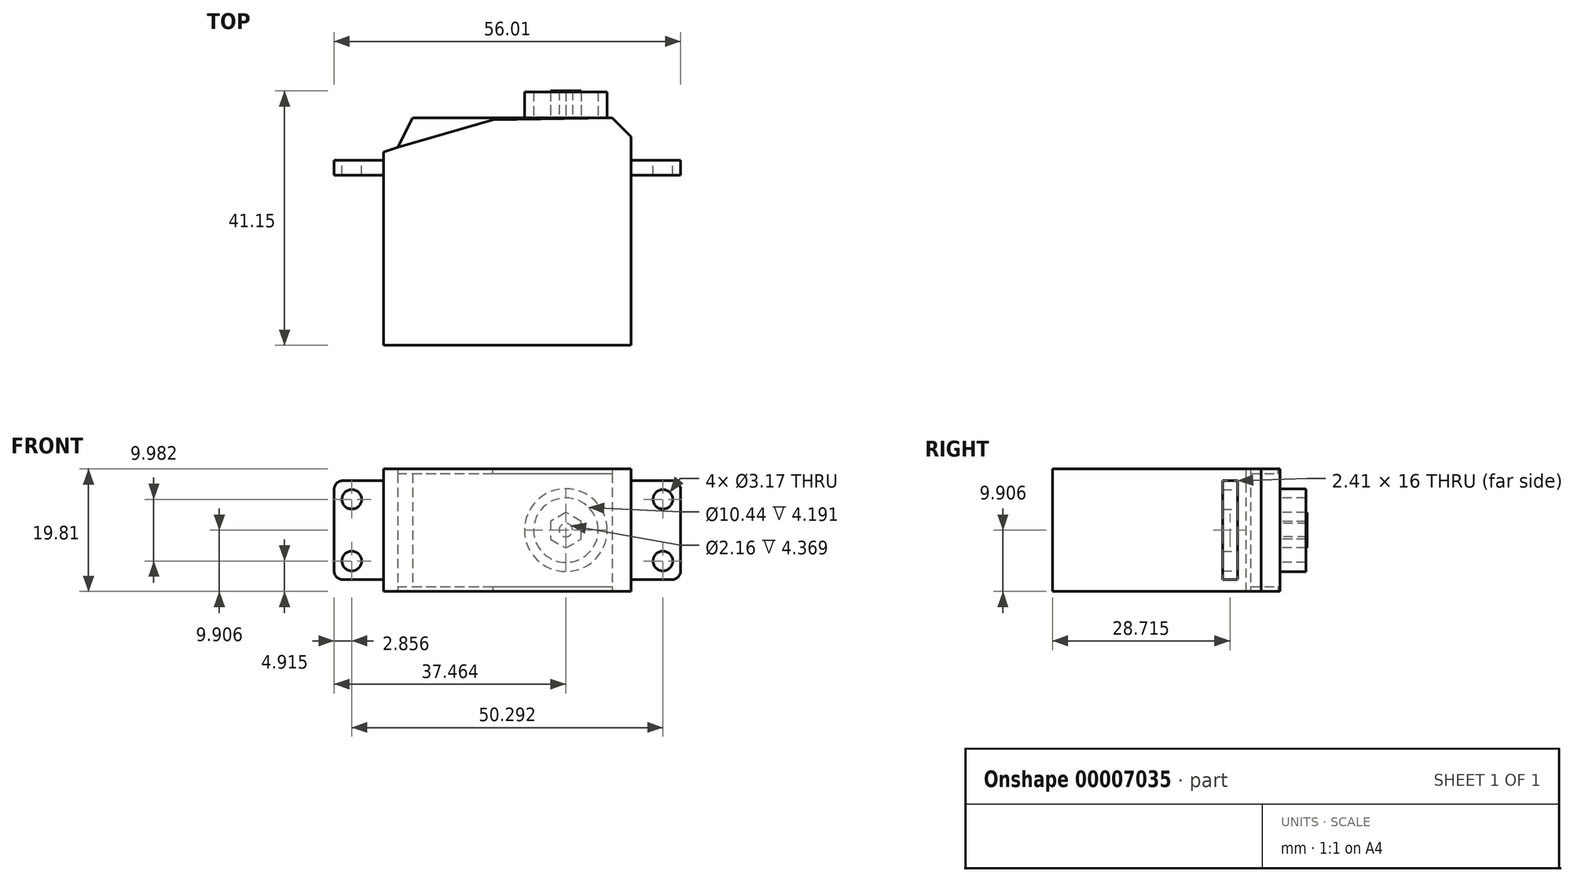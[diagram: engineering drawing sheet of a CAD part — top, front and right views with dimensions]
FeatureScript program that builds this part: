
annotation { "Feature Type Name" : "Feature", "Feature Type Description" : "" }
export const myFeature = defineFeature(function(context is Context, id is Id, definition is map)
    precondition{}
    {
        {
            var Q0;
            Q0=qCreatedBy(makeId("Top.planeOp"),FACE);
            var sketch = newSketch(context, id + "F0", { "sketchPlane" : qUnion([Q0])});
            skLineSegment(sketch, "E0.bottom", {"start": v(0, 0) * mm, "end": v(40, 0) * mm});
            skLineSegment(sketch, "E0.top", {"start": v(0, -36.78) * mm, "end": v(40, -36.78) * mm});
            skLineSegment(sketch, "E0.left", {"start": v(0, 0) * mm, "end": v(0, -36.78) * mm});
            skLineSegment(sketch, "E0.right", {"start": v(40, 0) * mm, "end": v(40, -36.78) * mm});
            skLineSegment(sketch, "E1", {"start": v(0, -5.54) * mm, "end": v(15.88, 0) * mm});
            skLineSegment(sketch, "E2", {"start": v(2.27, -4.75) * mm, "end": v(4.7, 0) * mm});
            skSolve(sketch);
        }
        {
            var Q0;
            {var subQ3=sQuery(id+"F0.wireOp",EDGE,"E0.top");Q0=makeQuery(id+"F0.imprint","IMPRINT",FACE,{"disambiguationData":[TD([[makeQuery(id+"F0.imprint","IMPRINT",EDGE,{"derivedFrom":subQ3}),1.0]])]});}
            extrude(context, id + "F1", {"entities" : qUnion([Q0]), "depth" : 19.8 * mm});
        }
        {
            var Q0;
            Q0=makeQuery(id+"F1.opExtrude","SWEPT_EDGE",EDGE,{"disambiguationData":[OSD([sQuery(id+"F0.wireOp",EDGE,"E0.bottom"),sQuery(id+"F0.wireOp",EDGE,"E0.right")])]});
            chamfer(context, id + "F2", {"entities" : qUnion([Q0]), "width" : 3.05 * mm, "tangentPropagation" : true});
        }
        {
            var Q0;
            {var subQ0=sQuery(id+"F0.wireOp",EDGE,"E2");Q0=makeQuery(id+"F0.imprint","IMPRINT",FACE,{"disambiguationData":[TD([[makeQuery(id+"F0.imprint","IMPRINT",EDGE,{"derivedFrom":subQ0}),-1.0]])]});}
            extrude(context, id + "F3", {"entities" : qUnion([Q0]), "operationType" : NewBodyOperationType.ADD, "depth" : 19.8 * mm});
        }
        {
            var Q0;
            Q0=makeQuery(id+"F1.opExtrude","SWEPT_FACE",FACE,{"disambiguationData":[OSD([sQuery(id+"F0.wireOp",EDGE,"E0.right")])]});
            var sketch = newSketch(context, id + "F4", { "sketchPlane" : qUnion([Q0])});
            skLineSegment(sketch, "E3.bottom", {"start": v(-6.86, 17.9) * mm, "end": v(-9.27, 17.9) * mm});
            skLineSegment(sketch, "E3.top", {"start": v(-6.86, 1.9) * mm, "end": v(-9.27, 1.9) * mm});
            skLineSegment(sketch, "E3.left", {"start": v(-6.86, 17.9) * mm, "end": v(-6.86, 1.9) * mm});
            skLineSegment(sketch, "E3.right", {"start": v(-9.27, 17.9) * mm, "end": v(-9.27, 1.9) * mm});
            skLineSegment(sketch, "E4", {"start": v(-6.86, 9.9) * mm, "end": v(-9.27, 9.9) * mm, "construction": true});
            skLineSegment(sketch, "E5", {"start": v(-6.86, 0) * mm, "end": v(-6.86, 19.81) * mm, "construction": true});
            skSolve(sketch);
        }
        {
            var Q0;
            Q0 = qSketchRegion(id + "F4", true);
            extrude(context, id + "F5", {"entities" : qUnion([Q0]), "operationType" : NewBodyOperationType.ADD, "depth" : 8 * mm});
        }
        {
            var Q0;
            Q0=makeQuery(id+"F1.opExtrude","SWEPT_FACE",FACE,{"disambiguationData":[OSD([sQuery(id+"F0.wireOp",EDGE,"E0.left")])]});
            var sketch = newSketch(context, id + "F6", { "sketchPlane" : qUnion([Q0])});
            skLineSegment(sketch, "E6.bottom", {"start": v(6.86, 1.9) * mm, "end": v(9.27, 1.9) * mm});
            skLineSegment(sketch, "E6.top", {"start": v(6.86, 17.9) * mm, "end": v(9.27, 17.9) * mm});
            skLineSegment(sketch, "E6.left", {"start": v(6.86, 1.9) * mm, "end": v(6.86, 17.9) * mm});
            skLineSegment(sketch, "E6.right", {"start": v(9.27, 1.9) * mm, "end": v(9.27, 17.9) * mm});
            skLineSegment(sketch, "E7", {"start": v(9.27, 19.81) * mm, "end": v(9.27, 0) * mm, "construction": true});
            skPoint(sketch, "E8", {"position": v(9.27, 9.9) * mm});
            skSolve(sketch);
        }
        {
            var Q0;
            Q0 = qSketchRegion(id + "F6", true);
            extrude(context, id + "F7", {"entities" : qUnion([Q0]), "operationType" : NewBodyOperationType.ADD, "depth" : 8 * mm});
        }
        {
            var Q0;
            Q0=makeQuery(id+"F5.opExtrude","SWEPT_FACE",FACE,{"disambiguationData":[OSD([sQuery(id+"F4.wireOp",EDGE,"E3.left")])]});
            var sketch = newSketch(context, id + "F8", { "sketchPlane" : qUnion([Q0])});
            skCircle(sketch, "E9", {"center": v(-45.15, 14.9) * mm, "radius": 1.59 * mm});
            skCircle(sketch, "E10", {"center": v(-45.15, 4.91) * mm, "radius": 1.59 * mm});
            skCircle(sketch, "E11", {"center": v(5.14, 14.9) * mm, "radius": 1.59 * mm});
            skCircle(sketch, "E12", {"center": v(5.14, 4.91) * mm, "radius": 1.59 * mm});
            skSolve(sketch);
        }
        {
            var Q0;
            Q0 = qSketchRegion(id + "F8", true);
            extrude(context, id + "F9", {"entities" : qUnion([Q0]), "operationType" : NewBodyOperationType.REMOVE, "oppositeDirection" : true, "depth" : 25.4 * mm});
        }
        {
            var Q0;
            Q0 = qSketchRegion(id + "F8", true);
            extrude(context, id + "F10", {"entities" : qUnion([Q0]), "operationType" : NewBodyOperationType.REMOVE, "oppositeDirection" : true, "depth" : 25.4 * mm});
        }
        {
            var Q0;
            Q0=makeQuery(id+"F5.opExtrude","CAP_EDGE",EDGE,{"disambiguationData":[OSD([sQuery(id+"F4.wireOp",EDGE,"E3.bottom")])],"isStart":false});
            var Q1;
            Q1=makeQuery(id+"F5.opExtrude","CAP_EDGE",EDGE,{"disambiguationData":[OSD([sQuery(id+"F4.wireOp",EDGE,"E3.top")])],"isStart":false});
            var Q2;
            Q2=makeQuery(id+"F7.opExtrude","CAP_EDGE",EDGE,{"disambiguationData":[OSD([sQuery(id+"F6.wireOp",EDGE,"E6.bottom")])],"isStart":false});
            var Q3;
            Q3=makeQuery(id+"F7.opExtrude","CAP_EDGE",EDGE,{"disambiguationData":[OSD([sQuery(id+"F6.wireOp",EDGE,"E6.top")])],"isStart":false});
            fillet(context, id + "F11", {"entities" : qUnion([Q0, Q1, Q2, Q3]), "radius" : 1.4 * mm, "tangentPropagation" : true, "allowEdgeOverflow" : false});
        }
        {
            var Q0;
            {var subQ0=sQuery(id+"F0.wireOp",EDGE,"E0.bottom");var subQ1=sQuery(id+"F0.wireOp",EDGE,"E1");Q0=makeQuery(id+"F3.boolean.opBoolean","MERGE",FACE,{"derivedFrom":[makeQuery(id+"F1.opExtrude","CAP_FACE",FACE,{"disambiguationData":[OSD([subQ0,sQuery(id+"F0.wireOp",EDGE,"E0.top"),sQuery(id+"F0.wireOp",EDGE,"E0.left"),sQuery(id+"F0.wireOp",EDGE,"E0.right"),subQ1])],"isStart":false}),makeQuery(id+"F3.opExtrude","CAP_FACE",FACE,{"disambiguationData":[OSD([subQ0,subQ1,sQuery(id+"F0.wireOp",EDGE,"E2")])],"isStart":false})]});}
            var sketch = newSketch(context, id + "F12", { "sketchPlane" : qUnion([Q0])});
            skLineSegment(sketch, "E13", {"start": v(2.27, -4.75) * mm, "end": v(40, -4.75) * mm});
            skLineSegment(sketch, "E14", {"start": v(2.27, -4.75) * mm, "end": v(17.64, -0.3) * mm});
            skLineSegment(sketch, "E15", {"start": v(17.64, -0.3) * mm, "end": v(36.96, 0) * mm});
            skSolve(sketch);
        }
        {
            var Q0;
            Q0=makeQuery(id+"F12.imprint","IMPRINT",FACE,{"disambiguationData":[TD([[makeQuery(id+"F12.imprint","IMPRINT",EDGE,{"derivedFrom":sQuery(id+"F12.wireOp",EDGE,"E14")}),1.0]])]});
            extrude(context, id + "F13", {"entities" : qUnion([Q0]), "operationType" : NewBodyOperationType.REMOVE, "oppositeDirection" : true, "depth" : 0.76 * mm});
        }
        {
            var Q0;
            {var subQ0=sQuery(id+"F0.wireOp",EDGE,"E0.bottom");var subQ1=sQuery(id+"F0.wireOp",EDGE,"E1");Q0=makeQuery(id+"F3.boolean.opBoolean","MERGE",FACE,{"derivedFrom":[makeQuery(id+"F1.opExtrude","CAP_FACE",FACE,{"disambiguationData":[OSD([subQ0,sQuery(id+"F0.wireOp",EDGE,"E0.top"),sQuery(id+"F0.wireOp",EDGE,"E0.left"),sQuery(id+"F0.wireOp",EDGE,"E0.right"),subQ1])],"isStart":true}),makeQuery(id+"F3.opExtrude","CAP_FACE",FACE,{"disambiguationData":[OSD([subQ0,subQ1,sQuery(id+"F0.wireOp",EDGE,"E2")])],"isStart":true})]});}
            var sketch = newSketch(context, id + "F14", { "sketchPlane" : qUnion([Q0])});
            skLineSegment(sketch, "E16", {"start": v(2.27, 4.75) * mm, "end": v(40, 4.75) * mm});
            skLineSegment(sketch, "E17", {"start": v(2.27, 4.75) * mm, "end": v(17.64, 0.3) * mm});
            skLineSegment(sketch, "E18", {"start": v(17.64, 0.3) * mm, "end": v(36.96, 0) * mm});
            skSolve(sketch);
        }
        {
            var Q0;
            Q0=makeQuery(id+"F14.imprint","IMPRINT",FACE,{"disambiguationData":[TD([[makeQuery(id+"F14.imprint","IMPRINT",EDGE,{"derivedFrom":sQuery(id+"F14.wireOp",EDGE,"E17")}),-1.0]])]});
            extrude(context, id + "F15", {"entities" : qUnion([Q0]), "operationType" : NewBodyOperationType.REMOVE, "oppositeDirection" : true, "depth" : 0.76 * mm});
        }
        {
            var Q0;
            {var subQ0=sQuery(id+"F0.wireOp",EDGE,"E0.bottom");Q0=makeQuery(id+"F3.boolean.opBoolean","MERGE",FACE,{"derivedFrom":[makeQuery(id+"F1.opExtrude","SWEPT_FACE",FACE,{"disambiguationData":[OSD([subQ0])]}),makeQuery(id+"F3.opExtrude","SWEPT_FACE",FACE,{"disambiguationData":[OSD([subQ0])]})]});}
            var sketch = newSketch(context, id + "F16", { "sketchPlane" : qUnion([Q0])});
            skCircle(sketch, "E19", {"center": v(-29.46, 9.9) * mm, "radius": 9.14 * mm});
            skCircle(sketch, "E20", {"center": v(-29.46, 9.9) * mm, "radius": 6.7 * mm});
            skCircle(sketch, "E21", {"center": v(-29.46, 9.9) * mm, "radius": 5.22 * mm});
            skPoint(sketch, "E22.orphan", {"position": v(-29.46, 19.05) * mm});
            skPoint(sketch, "E23.orphan", {"position": v(-29.46, 0.76) * mm});
            skCircle(sketch, "E24.cCircle", {"center": v(-29.46, 9.9) * mm, "radius": 2.49 * mm, "construction": true});
            skLineSegment(sketch, "E24.0", {"start": v(-31.95, 8.47) * mm, "end": v(-31.95, 11.34) * mm});
            skLineSegment(sketch, "E24.1", {"start": v(-31.95, 11.34) * mm, "end": v(-29.46, 12.78) * mm});
            skLineSegment(sketch, "E24.2", {"start": v(-29.46, 12.78) * mm, "end": v(-26.97, 11.34) * mm});
            skLineSegment(sketch, "E24.3", {"start": v(-26.97, 11.34) * mm, "end": v(-26.97, 8.47) * mm});
            skLineSegment(sketch, "E24.4", {"start": v(-26.97, 8.47) * mm, "end": v(-29.46, 7.03) * mm});
            skLineSegment(sketch, "E24.5", {"start": v(-29.46, 7.03) * mm, "end": v(-31.95, 8.47) * mm});
            skPoint(sketch, "E24.0.midPoint", {"position": v(-31.95, 9.9) * mm});
            skCircle(sketch, "E25", {"center": v(-29.46, 9.9) * mm, "radius": 1.08 * mm});
            skSolve(sketch);
        }
        {
            var Q0;
            Q0=makeQuery(id+"F16.imprint","IMPRINT",FACE,{"disambiguationData":[TD([[makeQuery(id+"F16.imprint","IMPRINT",EDGE,{"derivedFrom":sQuery(id+"F16.wireOp",EDGE,"E20")}),1.0]])]});
            extrude(context, id + "F17", {"entities" : qUnion([Q0]), "operationType" : NewBodyOperationType.ADD, "depth" : 4.2 * mm});
        }
        {
            var Q0;
            Q0=makeQuery(id+"F16.imprint","IMPRINT",FACE,{"disambiguationData":[TD([[makeQuery(id+"F16.imprint","IMPRINT",EDGE,{"derivedFrom":sQuery(id+"F16.wireOp",EDGE,"E24.0")}),-1.0]])]});
            extrude(context, id + "F18", {"entities" : qUnion([Q0]), "operationType" : NewBodyOperationType.ADD, "depth" : 4.37 * mm});
        }
    });
